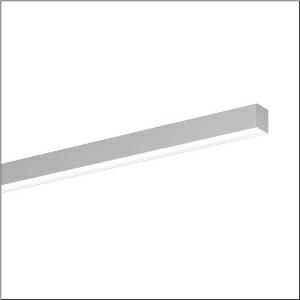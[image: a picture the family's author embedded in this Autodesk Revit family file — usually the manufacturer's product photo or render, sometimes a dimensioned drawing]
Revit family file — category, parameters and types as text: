
# Revit family: silica_21_51mx23db35sb
name_source: partatom
category: Lighting Fixtures
units: mm (PartAtom-declared; Revit-internal decimal feet)

## family parameters
Cut with Voids When Loaded = No
Host = Face
Light Source = No
Part Type = Normal
Room Calculation Point = No
Round Connector Dimension = Use Diameter
Shared = No

## types (1)
- --- (1 x LED, 4100 lm, 30.1 W, 3000K)
    Apparent Load = 30 VA
    CIE Flux Codes = 78 96 99 100 100
    Color Rendering = 80
    Color Temperature = 3000K
    Default Elevation = 1800 mm
    Description = Silica 21, office luminaire, primary optical cover: prismatic diffuser, of PMMA, CAT 2 (L<= 3000cd/m²), light emission: direct distribution, primary light characteristic: symmetric, installation type: surface-mounted, LED, rated luminous flux: 4.100lm, luminous efficacy: 136lm/W, light colour: 830, colour temperature: 3000K, control gear: DALI 2, with terminal, 3+2-pole, max. 2.5mm², mains connection: 220..240V, AC, 50/60Hz, rated input power: 30.1W, luminaire housing, of aluminium, metallic grey (RAL 9006), length: 1.504mm, width: 53mm, height: 53mm, protection rating (complete): IP20, insulation class (complete): insulation class I (protective earthing), certification: CE, permissible operating ambient temperature: 0..+35°C, standard: EN 50419, packaging unit: 1 piece
    Height = 53 mm
    Lamp = 1 x LED
    Lamp Light Flux = 4100 lm
    Lamp Power = 30.1 W
    Lamp count = 1
    Length = 1504 mm
    Luminous efficacy = 136 lm/W
    Manufacturer = Siteco
    ModVariant = No
    Model = 51MX23DB35SB
    Mounting Place = Ceiling
    Mounting Type = Surface mounted
    Number of Poles = 1
    OnlyDefault = Yes
    Power Factor = 1
    Product Name = Silica 21
    Product group = office luminaire | ceiling mounted
    ProductGroupID = 301
    Protection Class = Protection class I
    Protection Degree = IP 20
    RLX_Detail_Level = 1
    RLX_Emergency_Light_Flux = 0 lm
    RLX_Emergency_Type = 0
    RLX_Emergency_Type_DB = No
    RlxData = <blob elided: 21313 chars, md5=8bd4d59b>
    Socket = socket
    Standby Power = 0 W
    System Light Flux = 4100 lm
    System Power = 30 W
    Type Comments = factory setting: luminous flux: 100 % | dim-lin: 254 | 345 mA
    Type Image = l_1335933.jpg
    URL = http://relux.com
    VarID = @adj_119379
    Voltage = 0 V
    Weight = 0.00 kg
    Width = 53 mm

## geometry (parser evidence)
native form markers: Blend x4, Sweep x12
no freeform markers — native parametric forms only
